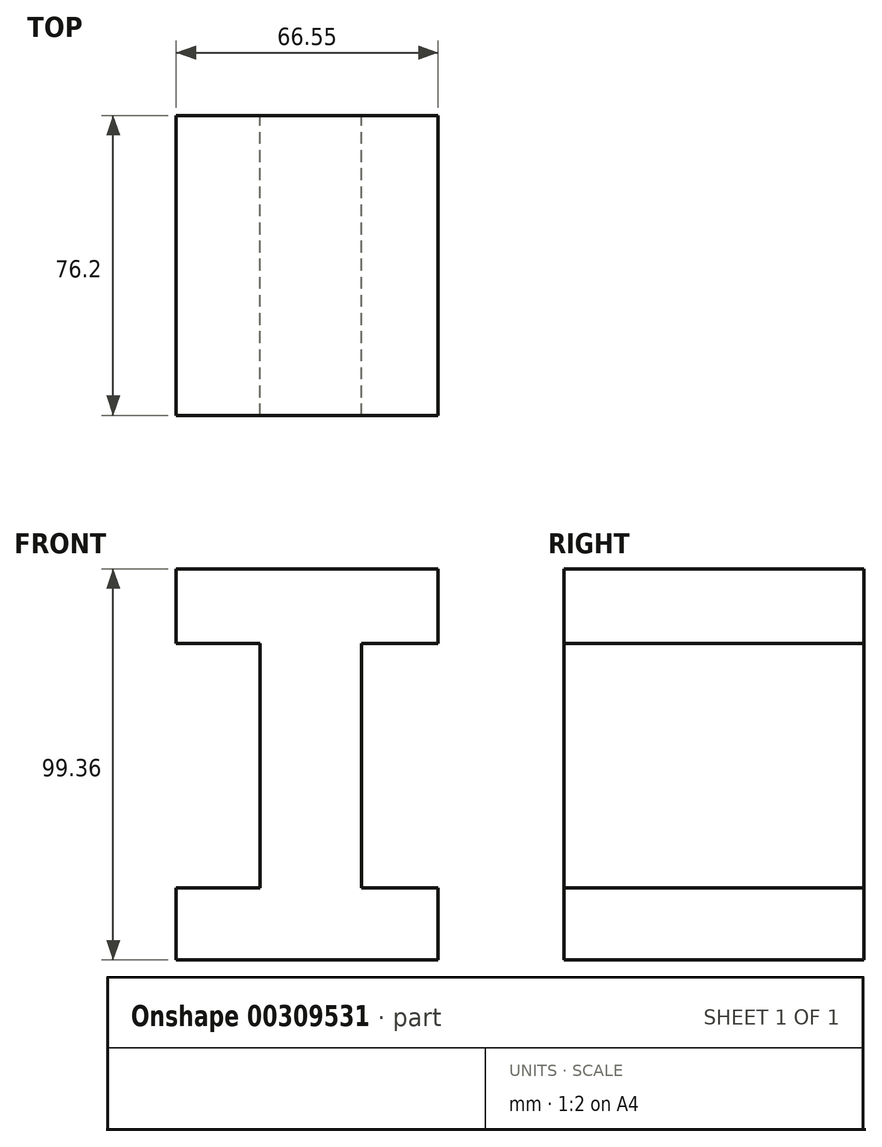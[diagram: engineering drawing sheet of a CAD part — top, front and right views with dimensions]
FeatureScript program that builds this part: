
annotation { "Feature Type Name" : "Feature", "Feature Type Description" : "" }
export const myFeature = defineFeature(function(context is Context, id is Id, definition is map)
    precondition{}
    {
        {
            var Q0;
            Q0=qCreatedBy(makeId("Front.planeOp"),FACE);
            var sketch = newSketch(context, id + "F0", { "sketchPlane" : qUnion([Q0])});
            skLineSegment(sketch, "E0", {"start": v(-34.67, -36.68) * mm, "end": v(31.88, -36.68) * mm});
            skLineSegment(sketch, "E1", {"start": v(31.88, -36.68) * mm, "end": v(31.88, -18.42) * mm});
            skLineSegment(sketch, "E2", {"start": v(31.88, -18.42) * mm, "end": v(12.38, -18.42) * mm});
            skLineSegment(sketch, "E3", {"start": v(12.38, -18.42) * mm, "end": v(12.38, 43.8) * mm});
            skLineSegment(sketch, "E4", {"start": v(12.38, 43.8) * mm, "end": v(31.88, 43.8) * mm});
            skLineSegment(sketch, "E5", {"start": v(31.88, 43.8) * mm, "end": v(31.88, 62.68) * mm});
            skLineSegment(sketch, "E6", {"start": v(31.88, 62.68) * mm, "end": v(-34.67, 62.68) * mm});
            skLineSegment(sketch, "E7", {"start": v(-34.67, 62.68) * mm, "end": v(-34.67, 43.8) * mm});
            skLineSegment(sketch, "E8", {"start": v(-34.67, 43.8) * mm, "end": v(-13.3, 43.8) * mm});
            skLineSegment(sketch, "E9", {"start": v(-13.3, 43.8) * mm, "end": v(-13.3, -18.42) * mm});
            skLineSegment(sketch, "E10", {"start": v(-13.3, -18.42) * mm, "end": v(-34.67, -18.42) * mm});
            skLineSegment(sketch, "E11", {"start": v(-34.67, -18.42) * mm, "end": v(-34.67, -36.68) * mm});
            skSolve(sketch);
        }
        {
            var Q0;
            Q0=qCreatedBy(makeId("Front.planeOp"),FACE);
            var sketch = newSketch(context, id + "F1", { "sketchPlane" : qUnion([Q0])});
            skSolve(sketch);
        }
        {
            var Q0;
            Q0 = qSketchRegion(id + "F1", true);
            var Q1;
            Q1=makeQuery(id+"F0.imprint","IMPRINT",FACE,{"disambiguationData":[TD([[makeQuery(id+"F0.imprint","IMPRINT",EDGE,{"derivedFrom":sQuery(id+"F0.wireOp",EDGE,"E0")}),1.0]])]});
            extrude(context, id + "F2", {"entities" : qUnion([Q0, Q1]), "depth" : 76.2 * mm});
        }
    });
